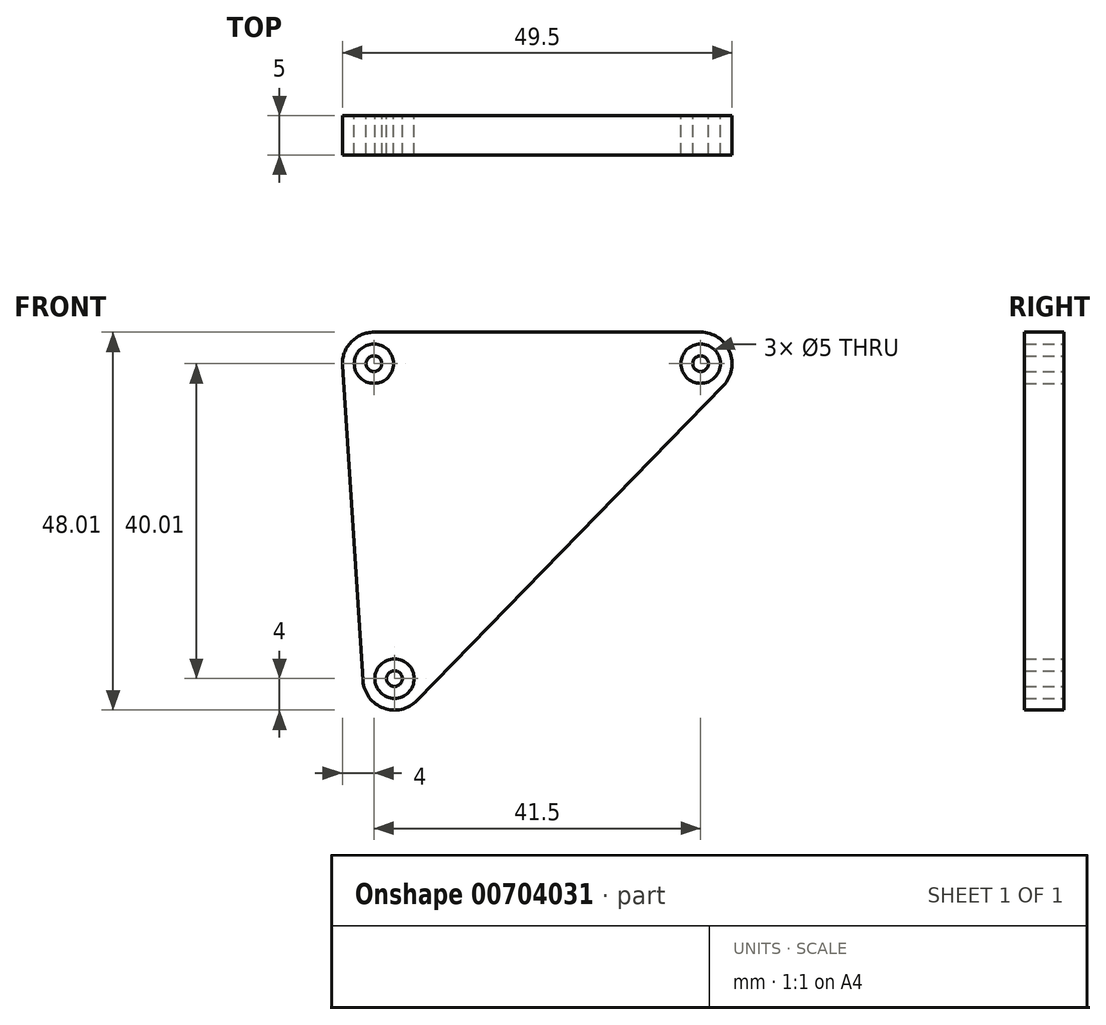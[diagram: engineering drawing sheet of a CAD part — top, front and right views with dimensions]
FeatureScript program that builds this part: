
annotation { "Feature Type Name" : "Feature", "Feature Type Description" : "" }
export const myFeature = defineFeature(function(context is Context, id is Id, definition is map)
    precondition{}
    {
        {
            var Q0;
            Q0=qCreatedBy(makeId("Front.planeOp"),FACE);
            var sketch = newSketch(context, id + "F0", { "sketchPlane" : qUnion([Q0])});
            skArc(sketch, "E0", {"start": v(-15.71, 6.74) * mm, "mid": v(-18.63, 5.47) * mm, "end": v(-19.7, 2.48) * mm});
            skArc(sketch, "E1", {"start": v(28.66, -0.05) * mm, "mid": v(29.47, 4.3) * mm, "end": v(25.79, 6.74) * mm});
            skArc(sketch, "E2", {"start": v(-17.1, -37.53) * mm, "mid": v(-14.48, -41.02) * mm, "end": v(-10.23, -40.06) * mm});
            skLineSegment(sketch, "E3", {"start": v(-19.7, 2.48) * mm, "end": v(-17.1, -37.53) * mm});
            skLineSegment(sketch, "E4", {"start": v(-10.23, -40.06) * mm, "end": v(28.66, -0.05) * mm});
            skLineSegment(sketch, "E5", {"start": v(-15.71, 6.74) * mm, "end": v(25.79, 6.74) * mm});
            skCircle(sketch, "E6", {"center": v(-15.71, 2.74) * mm, "radius": 2.5 * mm});
            skCircle(sketch, "E7", {"center": v(-13.1, -37.27) * mm, "radius": 2.5 * mm});
            skCircle(sketch, "E8", {"center": v(25.79, 2.74) * mm, "radius": 2.5 * mm});
            skCircle(sketch, "E9", {"center": v(-15.71, 2.74) * mm, "radius": 1 * mm});
            skCircle(sketch, "E10", {"center": v(-13.1, -37.27) * mm, "radius": 1 * mm});
            skCircle(sketch, "E11", {"center": v(25.79, 2.74) * mm, "radius": 1 * mm});
            skSolve(sketch);
        }
        {
            var Q0;
            Q0=makeQuery(id+"F0.imprint","IMPRINT",FACE,{"disambiguationData":[TD([[makeQuery(id+"F0.imprint","IMPRINT",EDGE,{"derivedFrom":sQuery(id+"F0.wireOp",EDGE,"E0")}),1.0]])]});
            var Q1;
            Q1=makeQuery(id+"F0.imprint","IMPRINT",FACE,{"disambiguationData":[TD([[makeQuery(id+"F0.imprint","IMPRINT",EDGE,{"derivedFrom":sQuery(id+"F0.wireOp",EDGE,"E9")}),1.0]])]});
            var Q2;
            Q2=makeQuery(id+"F0.imprint","IMPRINT",FACE,{"disambiguationData":[TD([[makeQuery(id+"F0.imprint","IMPRINT",EDGE,{"derivedFrom":sQuery(id+"F0.wireOp",EDGE,"E10")}),1.0]])]});
            var Q3;
            Q3=makeQuery(id+"F0.imprint","IMPRINT",FACE,{"disambiguationData":[TD([[makeQuery(id+"F0.imprint","IMPRINT",EDGE,{"derivedFrom":sQuery(id+"F0.wireOp",EDGE,"E11")}),1.0]])]});
            extrude(context, id + "F1", {"entities" : qUnion([Q0, Q1, Q2, Q3]), "depth" : 5 * mm, "offsetDistance" : 25 * mm});
        }
    });
